# Revit family: 230268MXG01-024_MGR6600PZ
name_source: partatom
category: Specialty Equipment
units: mm (PartAtom-declared; Revit-internal decimal feet)

## family parameters
Always vertical = Yes
Cut with Voids When Loaded = No
Enable Cutting in Views = No
Maintain Annotation Orientation = No
Part Type = Normal
Room Calculation Point = No
Round Connector Dimension = Use Diameter
Shared = No
Work Plane-Based = No

## types (1)
- MGR6600PZ
    Accent Material = ARCAT - Metal - Steel - Black
    Apparent Load = 0 VA
    Back Panel = ARCAT - Metal - Steel
    Body Material = ARCAT - Metal - Steel - Black Stainless
    Bolt Material = ARCAT - Metal - Steel - Coper
    Clearance Material = ARCAT - Clearance
    Default Elevation = 0"
    Depth = 0"
    Display Panel Material = ARCAT - Glass - Tempered - Black
    Display Unit = ARCAT - Metal - Steel - Black Stainless
    Door Front Panel Material = ARCAT - Metal - Steel - Stainless
    Door Material = ARCAT - Metal - Steel - Grey
    Family Name = 167898 167885 - Maytag
    Glass Material = ARCAT - Glass - Tempered - Black
    Height = 0"
    Knob = ARCAT - Metal - Steel
    Machine Material = ARCAT - Metal - Steel - light
    Voltage = 0 V
    Width = 0"

## geometry (parser evidence)
native form markers: Sweep x6
no freeform markers — native parametric forms only
